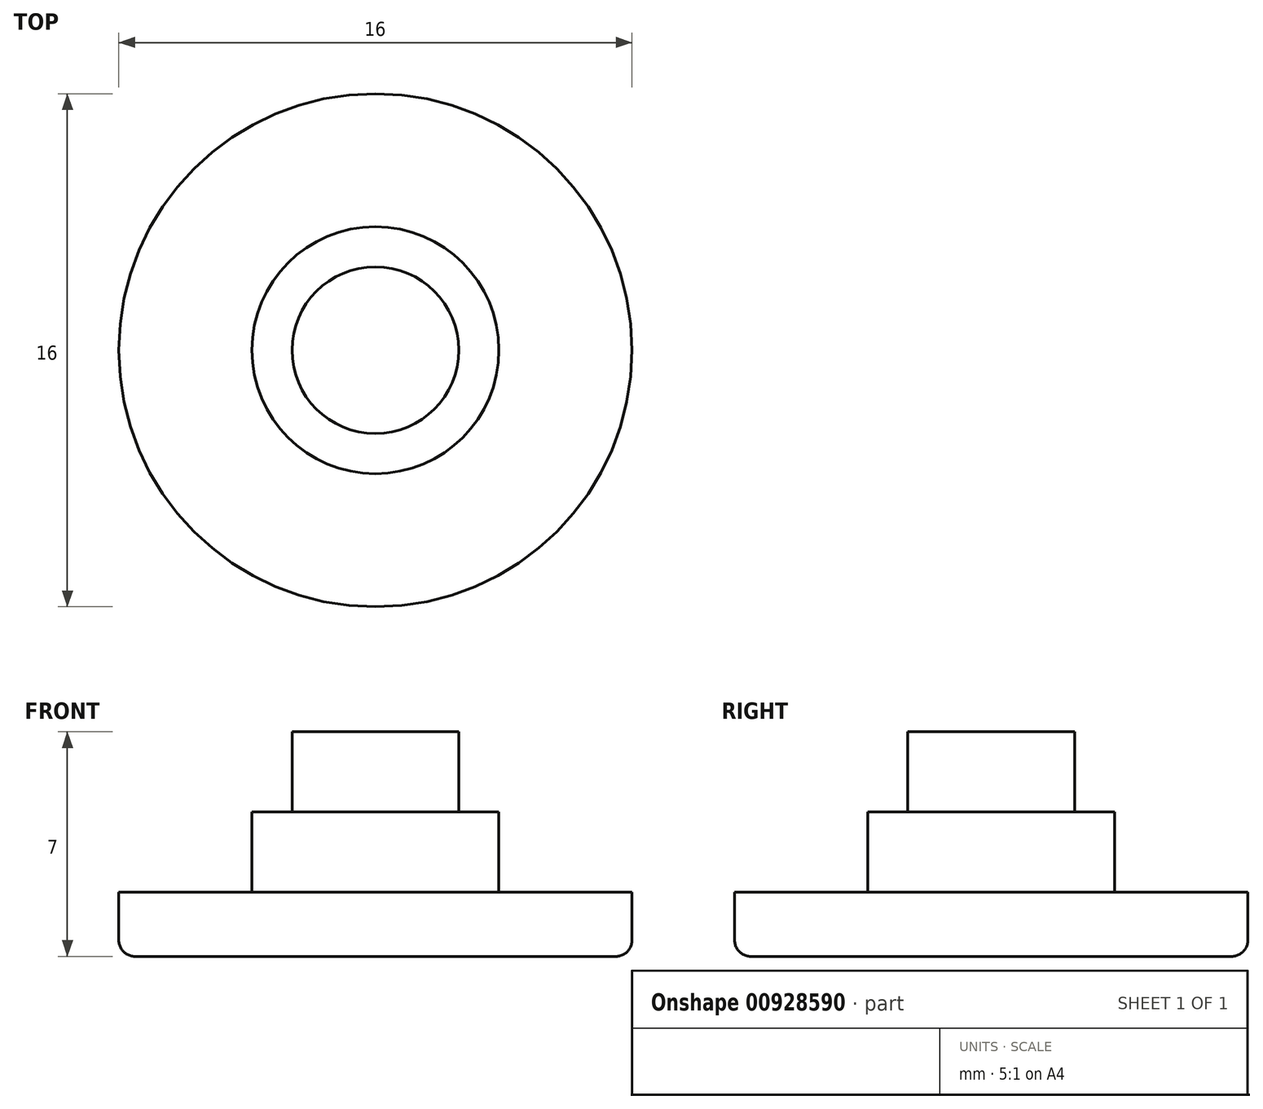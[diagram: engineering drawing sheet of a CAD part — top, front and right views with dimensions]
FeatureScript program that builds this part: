
annotation { "Feature Type Name" : "Feature", "Feature Type Description" : "" }
export const myFeature = defineFeature(function(context is Context, id is Id, definition is map)
    precondition{}
    {
        {
            var Q0;
            Q0=qCreatedBy(makeId("Front.planeOp"),FACE);
            var sketch = newSketch(context, id + "F0", { "sketchPlane" : qUnion([Q0])});
            skLineSegment(sketch, "E0", {"start": v(0, 5) * mm, "end": v(-2.6, 5) * mm});
            skLineSegment(sketch, "E1", {"start": v(-2.6, 5) * mm, "end": v(-2.6, 2.5) * mm});
            skLineSegment(sketch, "E2", {"start": v(-3.85, 0) * mm, "end": v(-8, 0) * mm});
            skLineSegment(sketch, "E3", {"start": v(-8, 0) * mm, "end": v(-8, -1.5) * mm});
            skLineSegment(sketch, "E4", {"start": v(-7.5, -2) * mm, "end": v(0, -2) * mm});
            skLineSegment(sketch, "E5", {"start": v(0, -2) * mm, "end": v(0, 5) * mm});
            skLineSegment(sketch, "E6", {"start": v(-3.85, 0) * mm, "end": v(-3.85, 2.5) * mm});
            skLineSegment(sketch, "E7", {"start": v(-3.85, 2.5) * mm, "end": v(-2.6, 2.5) * mm});
            skPoint(sketch, "E8.orphan", {"position": v(-2.6, 0) * mm});
            skPoint(sketch, "E9.visualSharp", {"position": v(-8, -2) * mm});
            skArc(sketch, "E9.filletArc", {"start": v(-8, -1.5) * mm, "mid": v(-7.85, -1.85) * mm, "end": v(-7.5, -2) * mm});
            skSolve(sketch);
        }
        {
            var Q0;
            Q0=qSketchRegion(id+"F0",true);
            var Q1;
            Q1=sQuery(id+"F0.wireOp",EDGE,"E5");
            revolve(context, id + "F1", {"surfaceOperationType" : NewSurfaceOperationType.NEW, "entities" : qUnion([Q0]), "axis" : qUnion([Q1]), "revolveType" : RevolveType.FULL});
        }
    });
